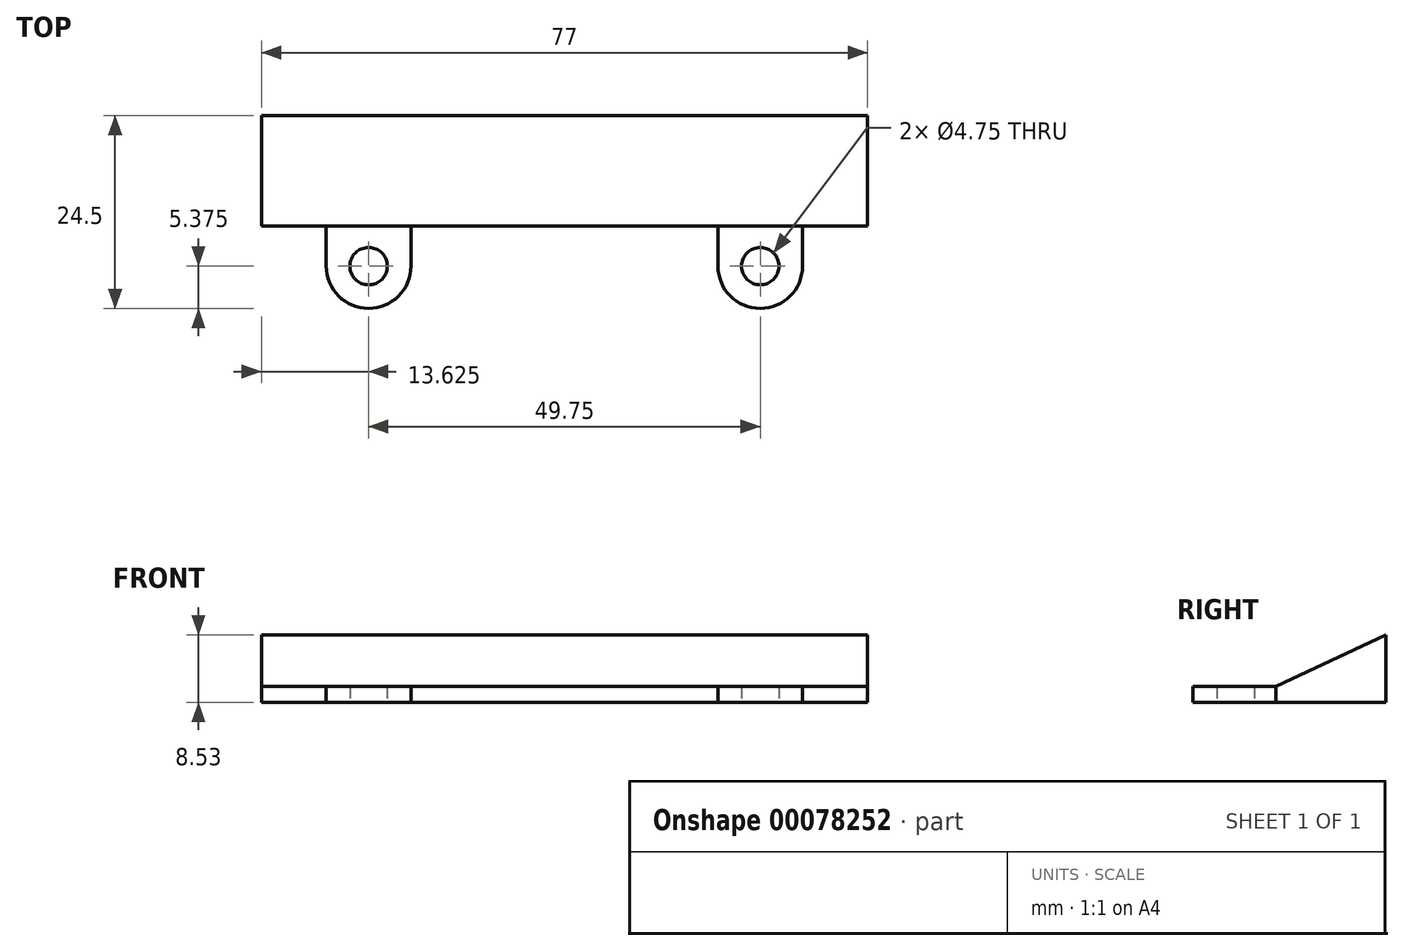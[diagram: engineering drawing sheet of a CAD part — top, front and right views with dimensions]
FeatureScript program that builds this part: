
annotation { "Feature Type Name" : "Feature", "Feature Type Description" : "" }
export const myFeature = defineFeature(function(context is Context, id is Id, definition is map)
    precondition{}
    {
        {
            var Q0;
            Q0=qCreatedBy(makeId("Top.planeOp"),FACE);
            var sketch = newSketch(context, id + "F0", { "sketchPlane" : qUnion([Q0])});
            skLineSegment(sketch, "E0.bottom", {"start": v(38.5, 7) * mm, "end": v(-38.5, 7) * mm});
            skLineSegment(sketch, "E0.top", {"start": v(38.5, -7) * mm, "end": v(30.25, -7) * mm});
            skLineSegment(sketch, "E0.left", {"start": v(38.5, 7) * mm, "end": v(38.5, -7) * mm});
            skLineSegment(sketch, "E0.right", {"start": v(-38.5, 7) * mm, "end": v(-38.5, -7) * mm});
            skPoint(sketch, "E0.middle", {"position": v(0, 0) * mm});
            skLineSegment(sketch, "E1", {"start": v(0, -7) * mm, "end": v(0, -12.13) * mm, "construction": true});
            skPoint(sketch, "E1.endSnap0", {"position": v(0, -7) * mm});
            skLineSegment(sketch, "E2", {"start": v(-24.88, -12.13) * mm, "end": v(24.88, -12.12) * mm, "construction": true});
            skCircle(sketch, "E3", {"center": v(-24.88, -12.12) * mm, "radius": 2.38 * mm});
            skCircle(sketch, "E4.MirrorC", {"center": v(24.88, -12.12) * mm, "radius": 2.38 * mm});
            skArc(sketch, "E5.0", {"start": v(-30.25, -12.13) * mm, "mid": v(-24.88, -17.5) * mm, "end": v(-19.5, -12.13) * mm});
            skLineSegment(sketch, "E6.trimOffspring", {"start": v(-30.25, -7) * mm, "end": v(-38.5, -7) * mm});
            skArc(sketch, "E7.0", {"start": v(30.25, -12.12) * mm, "mid": v(24.88, -17.5) * mm, "end": v(19.5, -12.13) * mm});
            skLineSegment(sketch, "E8.trimOffspring", {"start": v(19.5, -7) * mm, "end": v(-19.5, -7) * mm});
            skLineSegment(sketch, "E9", {"start": v(-19.5, -12.13) * mm, "end": v(-19.5, -7) * mm});
            skLineSegment(sketch, "E10", {"start": v(-30.25, -12.13) * mm, "end": v(-30.25, -7) * mm});
            skLineSegment(sketch, "E11", {"start": v(19.5, -12.13) * mm, "end": v(19.5, -7) * mm});
            skLineSegment(sketch, "E12", {"start": v(30.25, -12.12) * mm, "end": v(30.25, -7) * mm});
            skSolve(sketch);
        }
        {
            var Q0;
            Q0 = qSketchRegion(id + "F0", true);
            extrude(context, id + "F1", {"entities" : qUnion([Q0]), "depth" : 2 * mm});
        }
        {
            var Q0;
            Q0=makeQuery(id+"F1.opExtrude","SWEPT_FACE",FACE,{"disambiguationData":[OSD([sQuery(id+"F0.wireOp",EDGE,"E0.left")])]});
            var sketch = newSketch(context, id + "F2", { "sketchPlane" : qUnion([Q0])});
            skLineSegment(sketch, "E13", {"start": v(-7, 2) * mm, "end": v(7, 2) * mm});
            skLineSegment(sketch, "E14", {"start": v(-7, 2) * mm, "end": v(7, 8.53) * mm});
            skLineSegment(sketch, "E15", {"start": v(7, 2) * mm, "end": v(7, 8.53) * mm});
            skSolve(sketch);
        }
        {
            var Q0;
            Q0 = qSketchRegion(id + "F2", true);
            var Q1;
            Q1=makeQuery(id+"F1.opExtrude","SWEPT_FACE",FACE,{"disambiguationData":[OSD([sQuery(id+"F0.wireOp",EDGE,"E0.right")])]});
            extrude(context, id + "F3", {"entities" : qUnion([Q0]), "operationType" : NewBodyOperationType.ADD, "endBound" : BoundingType.UP_TO_SURFACE, "oppositeDirection" : true, "endBoundEntityFace" : qUnion([Q1]), "depth" : 25 * mm});
        }
    });
